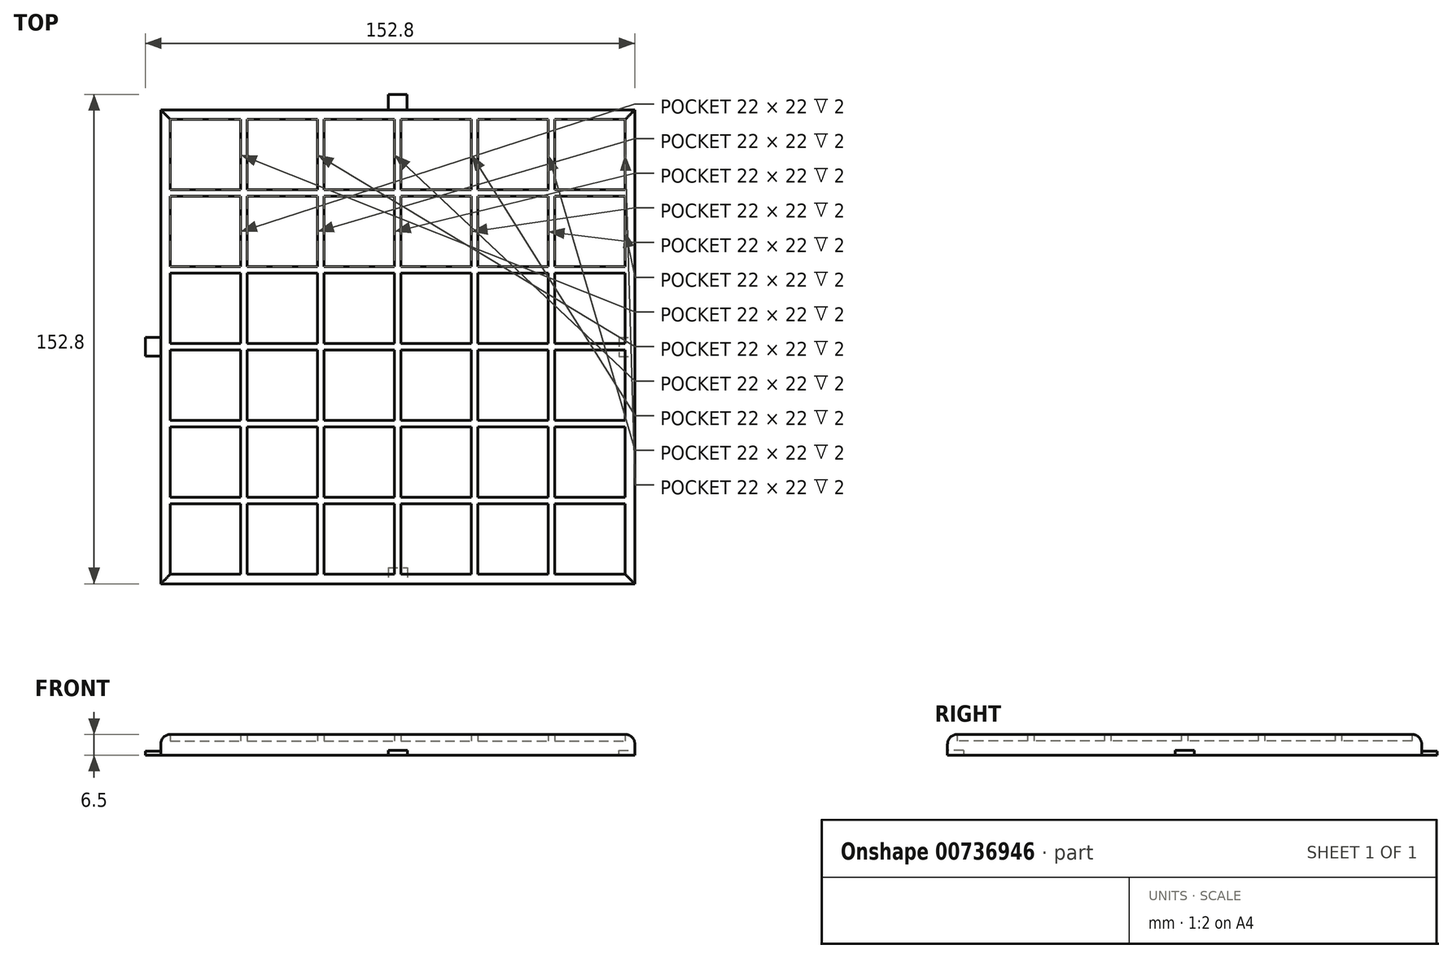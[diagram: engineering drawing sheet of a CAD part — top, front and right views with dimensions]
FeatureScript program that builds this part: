
annotation { "Feature Type Name" : "Feature", "Feature Type Description" : "" }
export const myFeature = defineFeature(function(context is Context, id is Id, definition is map)
    precondition{}
    {
        {
            var Q0;
            Q0=qCreatedBy(makeId("Top.planeOp"),FACE);
            var sketch = newSketch(context, id + "F0", { "sketchPlane" : qUnion([Q0])});
            skLineSegment(sketch, "E0.bottom", {"start": v(-74, 74) * mm, "end": v(74, 74) * mm});
            skLineSegment(sketch, "E0.top", {"start": v(-74, -74) * mm, "end": v(74, -74) * mm});
            skLineSegment(sketch, "E0.left", {"start": v(-74, 74) * mm, "end": v(-74, -74) * mm});
            skLineSegment(sketch, "E0.right", {"start": v(74, 74) * mm, "end": v(74, -74) * mm});
            skLineSegment(sketch, "E1.bottom", {"start": v(-71, 71) * mm, "end": v(71, 71) * mm});
            skLineSegment(sketch, "E1.top", {"start": v(-71, -71) * mm, "end": v(71, -71) * mm});
            skLineSegment(sketch, "E1.left", {"start": v(-71, 71) * mm, "end": v(-71, -71) * mm});
            skLineSegment(sketch, "E1.right", {"start": v(71, 71) * mm, "end": v(71, -71) * mm});
            skSolve(sketch);
        }
        {
            var Q0;
            Q0=qCreatedBy(makeId("Top.planeOp"),FACE);
            var sketch = newSketch(context, id + "F1", { "sketchPlane" : qUnion([Q0])});
            skLineSegment(sketch, "E2.bottom", {"start": v(-49, 71) * mm, "end": v(-47, 71) * mm});
            skLineSegment(sketch, "E2.top", {"start": v(-49, -71) * mm, "end": v(-47, -71) * mm});
            skLineSegment(sketch, "E2.left", {"start": v(-49, 71) * mm, "end": v(-49, -71) * mm});
            skLineSegment(sketch, "E2.right", {"start": v(-47, 71) * mm, "end": v(-47, -71) * mm});
            skLineSegment(sketch, "E3.1.0.0", {"start": v(-23, 71) * mm, "end": v(-23, -71) * mm});
            skLineSegment(sketch, "E3.1.0.1", {"start": v(-25, 71) * mm, "end": v(-25, -71) * mm});
            skLineSegment(sketch, "E3.1.0.2", {"start": v(-25, -71) * mm, "end": v(-23, -71) * mm});
            skLineSegment(sketch, "E3.2.0.0", {"start": v(1, 71) * mm, "end": v(1, -71) * mm});
            skLineSegment(sketch, "E3.2.0.1", {"start": v(-1, 71) * mm, "end": v(-1, -71) * mm});
            skLineSegment(sketch, "E3.2.0.2", {"start": v(-1, -71) * mm, "end": v(1, -71) * mm});
            skLineSegment(sketch, "E3.3.0.0", {"start": v(25, 71) * mm, "end": v(25, -71) * mm});
            skLineSegment(sketch, "E3.3.0.1", {"start": v(23, 71) * mm, "end": v(23, -71) * mm});
            skLineSegment(sketch, "E3.3.0.2", {"start": v(23, -71) * mm, "end": v(25, -71) * mm});
            skLineSegment(sketch, "E3.4.0.0", {"start": v(49, 71) * mm, "end": v(49, -71) * mm});
            skLineSegment(sketch, "E3.4.0.1", {"start": v(47, 71) * mm, "end": v(47, -71) * mm});
            skLineSegment(sketch, "E3.4.0.2", {"start": v(47, -71) * mm, "end": v(49, -71) * mm});
            skLineSegment(sketch, "E3.direction1", {"start": v(-49, -71) * mm, "end": v(-25, -71) * mm, "construction": true});
            skLineSegment(sketch, "E4", {"start": v(-25, 71) * mm, "end": v(-23, 71) * mm});
            skLineSegment(sketch, "E5", {"start": v(-1, 71) * mm, "end": v(1, 71) * mm});
            skLineSegment(sketch, "E6", {"start": v(23, 71) * mm, "end": v(25, 71) * mm});
            skLineSegment(sketch, "E7", {"start": v(49, 71) * mm, "end": v(47, 71) * mm});
            skSolve(sketch);
        }
        {
            var Q0;
            Q0=qCreatedBy(makeId("Top.planeOp"),FACE);
            var sketch = newSketch(context, id + "F2", { "sketchPlane" : qUnion([Q0])});
            skLineSegment(sketch, "E8.bottom", {"start": v(-71, 47) * mm, "end": v(71, 47) * mm});
            skLineSegment(sketch, "E8.top", {"start": v(-71, 49) * mm, "end": v(71, 49) * mm});
            skLineSegment(sketch, "E8.left", {"start": v(-71, 47) * mm, "end": v(-71, 49) * mm});
            skLineSegment(sketch, "E8.right", {"start": v(71, 47) * mm, "end": v(71, 49) * mm});
            skLineSegment(sketch, "E9.0.1.0", {"start": v(-71, 25) * mm, "end": v(71, 25) * mm});
            skLineSegment(sketch, "E9.0.1.1", {"start": v(-71, 23) * mm, "end": v(71, 23) * mm});
            skLineSegment(sketch, "E9.0.2.0", {"start": v(-71, 1) * mm, "end": v(71, 1) * mm});
            skLineSegment(sketch, "E9.0.2.1", {"start": v(-71, -1) * mm, "end": v(71, -1) * mm});
            skLineSegment(sketch, "E9.0.3.0", {"start": v(-71, -23) * mm, "end": v(71, -23) * mm});
            skLineSegment(sketch, "E9.0.3.1", {"start": v(-71, -25) * mm, "end": v(71, -25) * mm});
            skLineSegment(sketch, "E9.0.4.0", {"start": v(-71, -47) * mm, "end": v(71, -47) * mm});
            skLineSegment(sketch, "E9.0.4.1", {"start": v(-71, -49) * mm, "end": v(71, -49) * mm});
            skLineSegment(sketch, "E9.direction1", {"start": v(-71, 49) * mm, "end": v(-46, 49) * mm, "construction": true});
            skLineSegment(sketch, "E9.direction2", {"start": v(-71, 49) * mm, "end": v(-71, 25) * mm, "construction": true});
            skLineSegment(sketch, "E10", {"start": v(71, 25) * mm, "end": v(71, 23) * mm});
            skLineSegment(sketch, "E11", {"start": v(71, 1) * mm, "end": v(71, -1) * mm});
            skLineSegment(sketch, "E12", {"start": v(71, -23) * mm, "end": v(71, -25) * mm});
            skLineSegment(sketch, "E13", {"start": v(71, -47) * mm, "end": v(71, -49) * mm});
            skLineSegment(sketch, "E14", {"start": v(-71, 1) * mm, "end": v(-71, -1) * mm});
            skLineSegment(sketch, "E15", {"start": v(-71, -23) * mm, "end": v(-71, -25) * mm});
            skLineSegment(sketch, "E16", {"start": v(-71, -47) * mm, "end": v(-71, -49) * mm});
            skLineSegment(sketch, "E17", {"start": v(-71, 25) * mm, "end": v(-71, 23) * mm});
            skSolve(sketch);
        }
        {
            var Q0;
            Q0=makeQuery(id+"F1.imprint","IMPRINT",FACE,{"disambiguationData":[TD([[makeQuery(id+"F1.imprint","IMPRINT",EDGE,{"derivedFrom":sQuery(id+"F1.wireOp",EDGE,"E2.bottom")}),-1.0]])]});
            var Q1;
            Q1=makeQuery(id+"F0.imprint","IMPRINT",FACE,{"disambiguationData":[TD([[makeQuery(id+"F0.imprint","IMPRINT",EDGE,{"derivedFrom":sQuery(id+"F0.wireOp",EDGE,"E0.bottom")}),-1.0]])]});
            var Q2;
            Q2=sQuery(id+"F1.wireOp",EDGE,"E2.right");
            var Q3;
            Q3=sQuery(id+"F1.wireOp",EDGE,"E2.left");
            extrude(context, id + "F3", {"entities" : qUnion([Q0, Q1]), "surfaceEntities" : qUnion([Q2, Q3]), "depth" : 2 * mm, "offsetDistance" : 25 * mm});
        }
        {
            var Q0;
            Q0=qCreatedBy(makeId("Top.planeOp"),FACE);
            var sketch = newSketch(context, id + "F4", { "sketchPlane" : qUnion([Q0])});
            skLineSegment(sketch, "E18.bottom", {"start": v(-74, 74) * mm, "end": v(74, 74) * mm});
            skLineSegment(sketch, "E18.top", {"start": v(-74, -74) * mm, "end": v(74, -74) * mm});
            skLineSegment(sketch, "E18.left", {"start": v(-74, 74) * mm, "end": v(-74, -74) * mm});
            skLineSegment(sketch, "E18.right", {"start": v(74, 74) * mm, "end": v(74, -74) * mm});
            skSolve(sketch);
        }
        {
            var Q0;
            Q0 = qSketchRegion(id + "F2", true);
            extrude(context, id + "F5", {"entities" : qUnion([Q0]), "depth" : 2 * mm, "offsetDistance" : 25 * mm});
        }
        {
            var Q0;
            Q0 = qSketchRegion(id + "F1", true);
            extrude(context, id + "F6", {"entities" : qUnion([Q0]), "operationType" : NewBodyOperationType.ADD, "depth" : 2 * mm, "offsetDistance" : 25 * mm});
        }
        {
            var Q0;
            Q0 = qSketchRegion(id + "F4", true);
            extrude(context, id + "F7", {"entities" : qUnion([Q0]), "operationType" : NewBodyOperationType.ADD, "oppositeDirection" : true, "depth" : 4.5 * mm, "offsetDistance" : 25 * mm});
        }
        {
            var Q0;
            Q0=makeQuery(id+"F3.opExtrude","CAP_EDGE",EDGE,{"disambiguationData":[OSD([sQuery(id+"F0.wireOp",EDGE,"E0.bottom")])],"isStart":false});
            var Q1;
            Q1=makeQuery(id+"F3.opExtrude","CAP_EDGE",EDGE,{"disambiguationData":[OSD([sQuery(id+"F0.wireOp",EDGE,"E0.left")])],"isStart":false});
            var Q2;
            Q2=makeQuery(id+"F3.opExtrude","CAP_EDGE",EDGE,{"disambiguationData":[OSD([sQuery(id+"F0.wireOp",EDGE,"E0.top")])],"isStart":false});
            var Q3;
            Q3=makeQuery(id+"F3.opExtrude","CAP_EDGE",EDGE,{"disambiguationData":[OSD([sQuery(id+"F0.wireOp",EDGE,"E0.right")])],"isStart":false});
            fillet(context, id + "F8", {"entities" : qUnion([Q0, Q1, Q2, Q3]), "radius" : 3 * mm, "tangentPropagation" : true, "allowEdgeOverflow" : false});
        }
        {
            var Q0;
            Q0=makeQuery(id+"F7.boolean.opBoolean","MERGE",FACE,{"derivedFrom":[makeQuery(id+"F3.opExtrude","SWEPT_FACE",FACE,{"disambiguationData":[OSD([sQuery(id+"F0.wireOp",EDGE,"E0.right")])]}),makeQuery(id+"F7.opExtrude","SWEPT_FACE",FACE,{"disambiguationData":[OSD([sQuery(id+"F4.wireOp",EDGE,"E18.right")])]})]});
            var sketch = newSketch(context, id + "F9", { "sketchPlane" : qUnion([Q0])});
            skLineSegment(sketch, "E19.bottom", {"start": v(3, -4.5) * mm, "end": v(-3, -4.5) * mm});
            skLineSegment(sketch, "E19.top", {"start": v(3, -3) * mm, "end": v(-3, -3) * mm});
            skLineSegment(sketch, "E19.left", {"start": v(3, -4.5) * mm, "end": v(3, -3) * mm});
            skLineSegment(sketch, "E19.right", {"start": v(-3, -4.5) * mm, "end": v(-3, -3) * mm});
            skSolve(sketch);
        }
        {
            var Q0;
            Q0=makeQuery(id+"F9.imprint","IMPRINT",FACE,{"disambiguationData":[TD([[makeQuery(id+"F9.imprint","IMPRINT",EDGE,{"derivedFrom":sQuery(id+"F9.wireOp",EDGE,"E19.bottom")}),-1.0]])]});
            extrude(context, id + "F10", {"entities" : qUnion([Q0]), "operationType" : NewBodyOperationType.REMOVE, "oppositeDirection" : true, "depth" : 5 * mm, "offsetDistance" : 25 * mm});
        }
        {
            var Q0;
            Q0=makeQuery(id+"F7.boolean.opBoolean","MERGE",FACE,{"derivedFrom":[makeQuery(id+"F3.opExtrude","SWEPT_FACE",FACE,{"disambiguationData":[OSD([sQuery(id+"F0.wireOp",EDGE,"E0.top")])]}),makeQuery(id+"F7.opExtrude","SWEPT_FACE",FACE,{"disambiguationData":[OSD([sQuery(id+"F4.wireOp",EDGE,"E18.top")])]})]});
            var sketch = newSketch(context, id + "F11", { "sketchPlane" : qUnion([Q0])});
            skLineSegment(sketch, "E20.bottom", {"start": v(3, -3) * mm, "end": v(-3, -3) * mm});
            skLineSegment(sketch, "E20.top", {"start": v(3, -4.5) * mm, "end": v(-3, -4.5) * mm});
            skLineSegment(sketch, "E20.left", {"start": v(3, -3) * mm, "end": v(3, -4.5) * mm});
            skLineSegment(sketch, "E20.right", {"start": v(-3, -3) * mm, "end": v(-3, -4.5) * mm});
            skSolve(sketch);
        }
        {
            var Q0;
            Q0=makeQuery(id+"F11.imprint","IMPRINT",FACE,{"disambiguationData":[TD([[makeQuery(id+"F11.imprint","IMPRINT",EDGE,{"derivedFrom":sQuery(id+"F11.wireOp",EDGE,"E20.bottom")}),1.0]])]});
            extrude(context, id + "F12", {"entities" : qUnion([Q0]), "operationType" : NewBodyOperationType.REMOVE, "oppositeDirection" : true, "depth" : 5 * mm, "offsetDistance" : 25 * mm});
        }
        {
            var Q0;
            Q0=makeQuery(id+"F7.boolean.opBoolean","MERGE",FACE,{"derivedFrom":[makeQuery(id+"F3.opExtrude","SWEPT_FACE",FACE,{"disambiguationData":[OSD([sQuery(id+"F0.wireOp",EDGE,"E0.left")])]}),makeQuery(id+"F7.opExtrude","SWEPT_FACE",FACE,{"disambiguationData":[OSD([sQuery(id+"F4.wireOp",EDGE,"E18.left")])]})]});
            var sketch = newSketch(context, id + "F13", { "sketchPlane" : qUnion([Q0])});
            skLineSegment(sketch, "E21.bottom", {"start": v(-2.9, -4.5) * mm, "end": v(2.9, -4.5) * mm});
            skLineSegment(sketch, "E21.top", {"start": v(-2.9, -3.2) * mm, "end": v(2.9, -3.2) * mm});
            skLineSegment(sketch, "E21.left", {"start": v(-2.9, -4.5) * mm, "end": v(-2.9, -3.2) * mm});
            skLineSegment(sketch, "E21.right", {"start": v(2.9, -4.5) * mm, "end": v(2.9, -3.2) * mm});
            skSolve(sketch);
        }
        {
            var Q0;
            Q0 = qSketchRegion(id + "F13", true);
            extrude(context, id + "F14", {"entities" : qUnion([Q0]), "operationType" : NewBodyOperationType.ADD, "depth" : 4.8 * mm, "offsetDistance" : 25 * mm});
        }
        {
            var Q0;
            Q0=makeQuery(id+"F7.boolean.opBoolean","MERGE",FACE,{"derivedFrom":[makeQuery(id+"F3.opExtrude","SWEPT_FACE",FACE,{"disambiguationData":[OSD([sQuery(id+"F0.wireOp",EDGE,"E0.bottom")])]}),makeQuery(id+"F7.opExtrude","SWEPT_FACE",FACE,{"disambiguationData":[OSD([sQuery(id+"F4.wireOp",EDGE,"E18.bottom")])]})]});
            var sketch = newSketch(context, id + "F15", { "sketchPlane" : qUnion([Q0])});
            skLineSegment(sketch, "E22.bottom", {"start": v(-2.9, -4.5) * mm, "end": v(2.9, -4.5) * mm});
            skLineSegment(sketch, "E22.top", {"start": v(-2.9, -3.2) * mm, "end": v(2.9, -3.2) * mm});
            skLineSegment(sketch, "E22.left", {"start": v(-2.9, -4.5) * mm, "end": v(-2.9, -3.2) * mm});
            skLineSegment(sketch, "E22.right", {"start": v(2.9, -4.5) * mm, "end": v(2.9, -3.2) * mm});
            skSolve(sketch);
        }
        {
            var Q0;
            Q0 = qSketchRegion(id + "F15", true);
            extrude(context, id + "F16", {"entities" : qUnion([Q0]), "operationType" : NewBodyOperationType.ADD, "depth" : 4.8 * mm, "offsetDistance" : 25 * mm});
        }
    });
